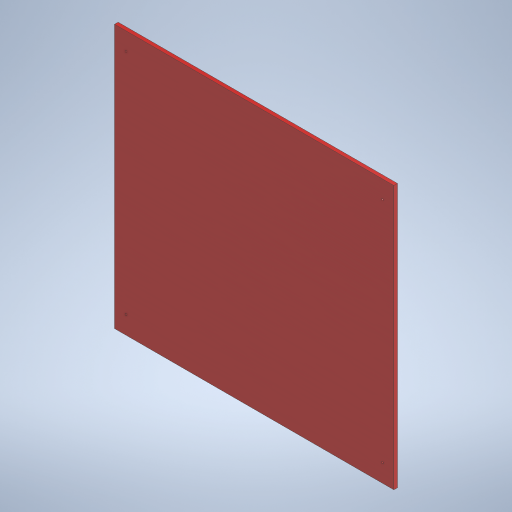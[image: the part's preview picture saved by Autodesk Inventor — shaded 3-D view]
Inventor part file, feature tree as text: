
AUTODESK INVENTOR PART (.ipt)
format: ipt  version: 2023.2 (Build 272271030, 271C)  size: 238,080 bytes
history: native  units: mm
features: extrude x1, sketch x1
ambient origin geometry x8: Origin, YZ Plane, XZ Plane, XY Plane, X Axis, Y Axis, Z Axis, Center Point
bodies: Solid1 (feature_tree)
feature tree (2):
  extrude  "Extrusion1"  Depth=780.0mm
  sketch  "Sketch1"  dims[d0=736.0mm d1=780.0mm d2=5.1mm d3=317.8995mm d4=715.999mm d5=10.0mm d6=0.0mm]
